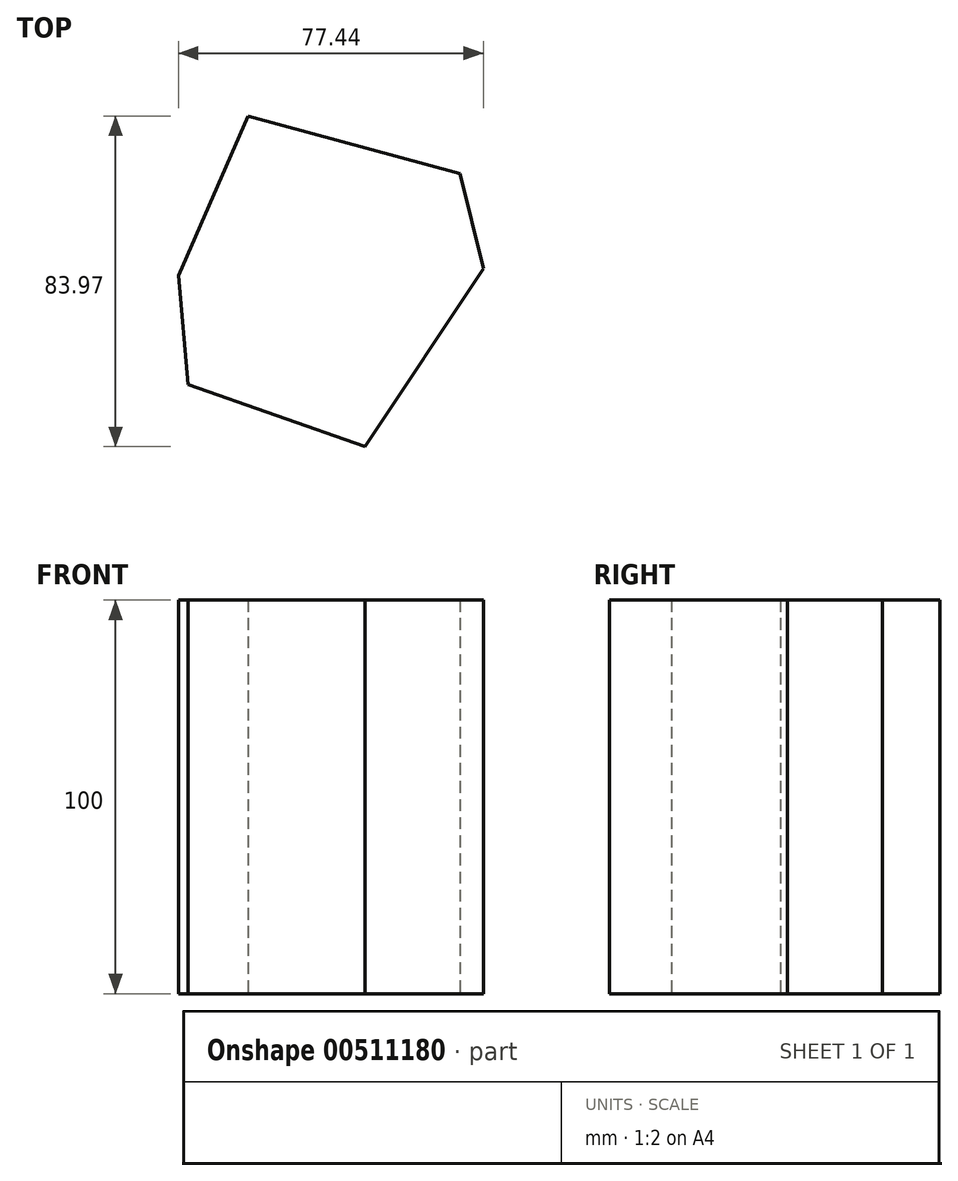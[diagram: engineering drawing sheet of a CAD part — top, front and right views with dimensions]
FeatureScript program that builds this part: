
annotation { "Feature Type Name" : "Feature", "Feature Type Description" : "" }
export const myFeature = defineFeature(function(context is Context, id is Id, definition is map)
    precondition{}
    {
        {
            var Q0;
            Q0=qCreatedBy(makeId("Top.planeOp"),FACE);
            var sketch = newSketch(context, id + "F0", { "sketchPlane" : qUnion([Q0])});
            skLineSegment(sketch, "E0", {"start": v(-41.68, 32.86) * mm, "end": v(12.17, 18.25) * mm});
            skLineSegment(sketch, "E1", {"start": v(12.17, 18.25) * mm, "end": v(-11.86, -21.6) * mm});
            skLineSegment(sketch, "E2", {"start": v(-41.68, 32.86) * mm, "end": v(-59.32, -7.6) * mm});
            skLineSegment(sketch, "E3", {"start": v(-59.32, -7.6) * mm, "end": v(-11.86, -21.6) * mm});
            skLineSegment(sketch, "E4", {"start": v(-33.77, 10.95) * mm, "end": v(18.56, -5.17) * mm});
            skLineSegment(sketch, "E5", {"start": v(18.56, -5.17) * mm, "end": v(-11.86, -51.1) * mm});
            skLineSegment(sketch, "E6", {"start": v(-33.77, 10.95) * mm, "end": v(-56.89, -35.29) * mm});
            skLineSegment(sketch, "E7", {"start": v(-56.89, -35.29) * mm, "end": v(-11.86, -51.1) * mm});
            skLineSegment(sketch, "E8", {"start": v(-41.68, 32.86) * mm, "end": v(-33.77, 10.95) * mm});
            skLineSegment(sketch, "E9", {"start": v(-59.32, -7.6) * mm, "end": v(-56.89, -35.29) * mm});
            skLineSegment(sketch, "E10", {"start": v(12.17, 18.25) * mm, "end": v(18.56, -7.6) * mm});
            skLineSegment(sketch, "E11", {"start": v(-12.47, -21.9) * mm, "end": v(-11.86, -51.1) * mm});
            skLineSegment(sketch, "E12", {"start": v(-33.77, 10.95) * mm, "end": v(-11.86, -21.6) * mm});
            skSolve(sketch);
        }
        {
            var Q0;
            {var subQ0=sQuery(id+"F0.wireOp",EDGE,"E12");Q0=makeQuery(id+"F0.imprint","IMPRINT",FACE,{"disambiguationData":[TD([[makeQuery(id+"F0.imprint","IMPRINT",EDGE,{"derivedFrom":subQ0}),-1.0]])]});}
            var Q1;
            {var subQ0=sQuery(id+"F0.wireOp",EDGE,"E0");Q1=makeQuery(id+"F0.imprint","IMPRINT",FACE,{"disambiguationData":[TD([[makeQuery(id+"F0.imprint","IMPRINT",EDGE,{"derivedFrom":subQ0}),-1.0]])]});}
            var Q2;
            {var subQ0=sQuery(id+"F0.wireOp",EDGE,"E10");var subQ3=sQuery(id+"F0.wireOp",EDGE,"E4");var subQ5=makeQuery(id+"F0.imprint","INTERSECT",VERTEX,{"derivedFrom":[subQ3,subQ0]});Q2=makeQuery(id+"F0.imprint","IMPRINT",FACE,{"disambiguationData":[TD([[makeQuery(id+"F0.imprint","IMPRINT",EDGE,{"disambiguationData":[TD([[subQ5,1.0]])],"derivedFrom":subQ3}),1.0]])]});}
            var Q3;
            {var subQ0=sQuery(id+"F0.wireOp",EDGE,"E9");Q3=makeQuery(id+"F0.imprint","IMPRINT",FACE,{"disambiguationData":[TD([[makeQuery(id+"F0.imprint","IMPRINT",EDGE,{"derivedFrom":subQ0}),1.0]])]});}
            var Q4;
            {var subQ0=sQuery(id+"F0.wireOp",EDGE,"E2");Q4=makeQuery(id+"F0.imprint","IMPRINT",FACE,{"disambiguationData":[TD([[makeQuery(id+"F0.imprint","IMPRINT",EDGE,{"derivedFrom":subQ0}),1.0]])]});}
            var Q5;
            {var subQ0=sQuery(id+"F0.wireOp",EDGE,"E12");Q5=makeQuery(id+"F0.imprint","IMPRINT",FACE,{"disambiguationData":[TD([[makeQuery(id+"F0.imprint","IMPRINT",EDGE,{"derivedFrom":subQ0}),1.0]])]});}
            var Q6;
            {var subQ0=sQuery(id+"F0.wireOp",EDGE,"E7");Q6=makeQuery(id+"F0.imprint","IMPRINT",FACE,{"disambiguationData":[TD([[makeQuery(id+"F0.imprint","IMPRINT",EDGE,{"derivedFrom":subQ0}),1.0]])]});}
            extrude(context, id + "F1", {"entities" : qUnion([Q0, Q1, Q2, Q3, Q4, Q5, Q6]), "depth" : 100 * mm});
        }
    });
